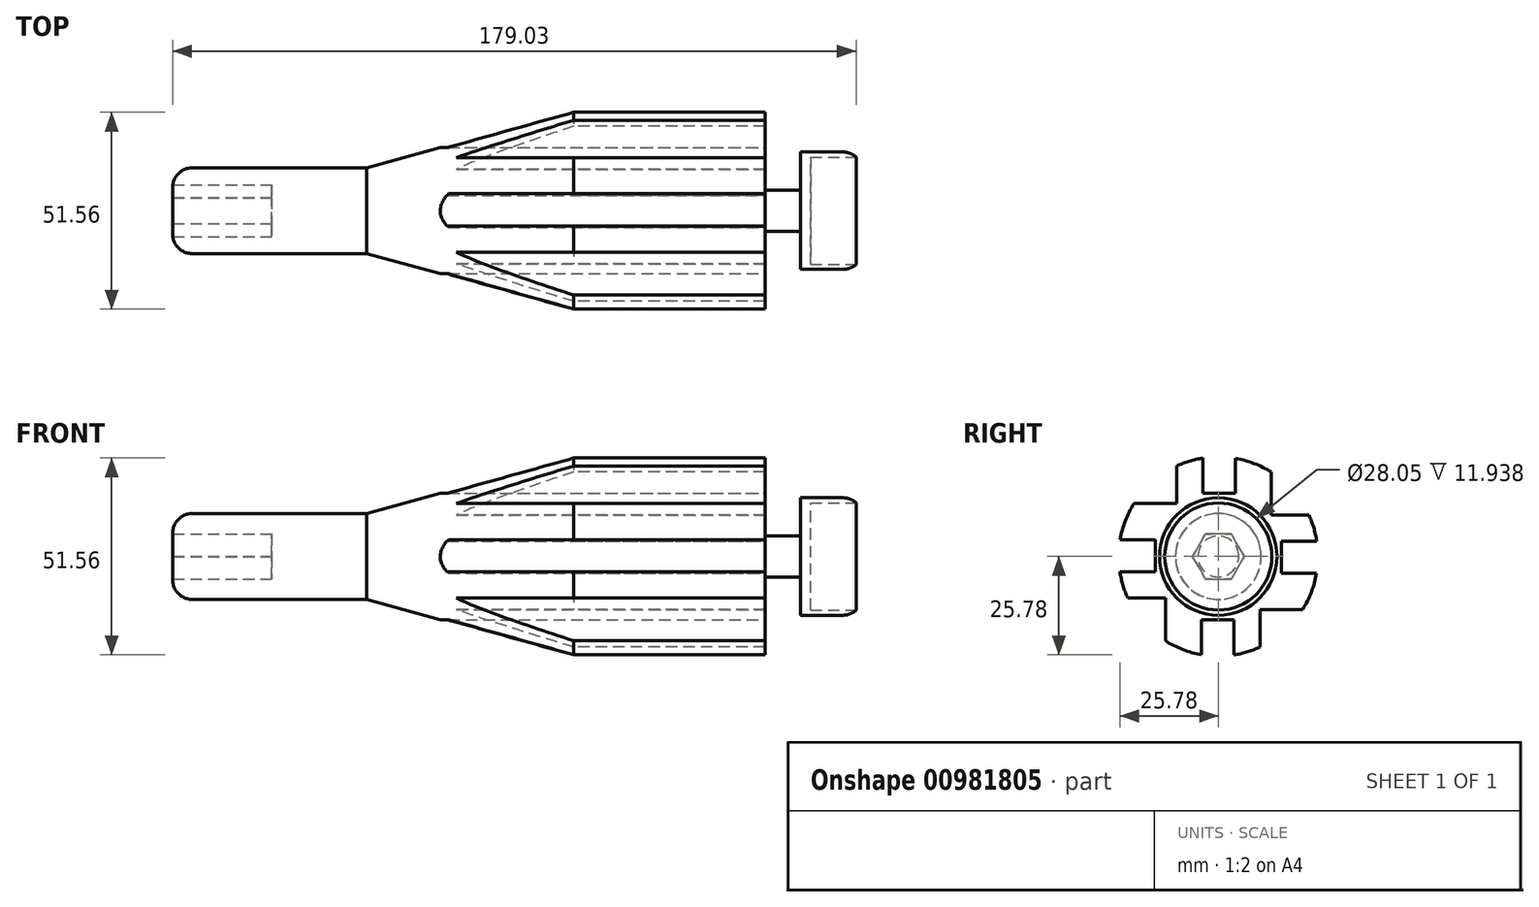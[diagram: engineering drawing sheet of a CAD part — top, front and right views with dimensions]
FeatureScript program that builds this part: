
annotation { "Feature Type Name" : "Feature", "Feature Type Description" : "" }
export const myFeature = defineFeature(function(context is Context, id is Id, definition is map)
    precondition{}
    {
        {
            var Q0;
            Q0=qCreatedBy(makeId("Front.planeOp"),FACE);
            var sketch = newSketch(context, id + "F0", { "sketchPlane" : qUnion([Q0])});
            skLineSegment(sketch, "E0", {"start": v(-55.13, 0) * mm, "end": v(-55.13, 11.23) * mm});
            skLineSegment(sketch, "E1", {"start": v(-55.13, 11.23) * mm, "end": v(-30.24, 11.23) * mm});
            skLineSegment(sketch, "E2", {"start": v(-30.24, 11.23) * mm, "end": v(24.02, 26.1) * mm});
            skLineSegment(sketch, "E3", {"start": v(24.02, 26.1) * mm, "end": v(74.14, 26.1) * mm});
            skLineSegment(sketch, "E4", {"start": v(74.14, 26.1) * mm, "end": v(74.14, 5.36) * mm});
            skLineSegment(sketch, "E5", {"start": v(74.14, 5.36) * mm, "end": v(83.47, 5.36) * mm});
            skLineSegment(sketch, "E6", {"start": v(83.47, 5.36) * mm, "end": v(83.47, 15.38) * mm});
            skLineSegment(sketch, "E7", {"start": v(83.47, 15.38) * mm, "end": v(97.99, 15.38) * mm});
            skLineSegment(sketch, "E8", {"start": v(97.99, 15.38) * mm, "end": v(97.99, 0) * mm});
            skLineSegment(sketch, "E9", {"start": v(-78.98, 0) * mm, "end": v(111.47, 0) * mm, "construction": true});
            skLineSegment(sketch, "E10", {"start": v(-55.13, 0) * mm, "end": v(97.99, 0) * mm});
            skSolve(sketch);
        }
        {
            var Q0;
            Q0=makeQuery(id+"F0.imprint","IMPRINT",FACE,{"disambiguationData":[TD([[makeQuery(id+"F0.imprint","IMPRINT",EDGE,{"derivedFrom":sQuery(id+"F0.wireOp",EDGE,"E0")}),-1.0]])]});
            var Q1;
            Q1=sQuery(id+"F0.wireOp",EDGE,"E9");
            revolve(context, id + "F1", {"surfaceOperationType" : NewSurfaceOperationType.NEW, "entities" : qUnion([Q0]), "axis" : qUnion([Q1]), "revolveType" : RevolveType.FULL});
        }
        {
            var Q0;
            Q0=makeQuery(id+"F1.opRevolve","SWEPT_FACE",FACE,{"disambiguationData":[OSD([sQuery(id+"F0.wireOp",EDGE,"E4")])]});
            var sketch = newSketch(context, id + "F2", { "sketchPlane" : qUnion([Q0])});
            skLineSegment(sketch, "E11.bottom", {"start": v(-4.05, 28.22) * mm, "end": v(4.44, 28.22) * mm});
            skLineSegment(sketch, "E11.top", {"start": v(-4.05, 16.52) * mm, "end": v(4.44, 16.52) * mm});
            skLineSegment(sketch, "E11.left", {"start": v(-4.05, 28.22) * mm, "end": v(-4.05, 16.52) * mm});
            skLineSegment(sketch, "E11.right", {"start": v(4.44, 28.22) * mm, "end": v(4.44, 16.52) * mm});
            skLineSegment(sketch, "E12.1.0", {"start": v(-28.22, -4.05) * mm, "end": v(-28.22, 4.44) * mm});
            skLineSegment(sketch, "E12.1.1", {"start": v(-16.52, -4.05) * mm, "end": v(-16.52, 4.44) * mm});
            skLineSegment(sketch, "E12.1.2", {"start": v(-28.22, 4.44) * mm, "end": v(-16.52, 4.44) * mm});
            skLineSegment(sketch, "E12.1.3", {"start": v(-28.22, -4.05) * mm, "end": v(-16.52, -4.05) * mm});
            skLineSegment(sketch, "E12.2.0", {"start": v(4.05, -28.22) * mm, "end": v(-4.44, -28.22) * mm});
            skLineSegment(sketch, "E12.2.1", {"start": v(4.05, -16.52) * mm, "end": v(-4.44, -16.52) * mm});
            skLineSegment(sketch, "E12.2.2", {"start": v(-4.44, -28.22) * mm, "end": v(-4.44, -16.52) * mm});
            skLineSegment(sketch, "E12.2.3", {"start": v(4.05, -28.22) * mm, "end": v(4.05, -16.52) * mm});
            skLineSegment(sketch, "E12.3.0", {"start": v(28.22, 4.05) * mm, "end": v(28.22, -4.44) * mm});
            skLineSegment(sketch, "E12.3.1", {"start": v(16.52, 4.05) * mm, "end": v(16.52, -4.44) * mm});
            skLineSegment(sketch, "E12.3.2", {"start": v(28.22, -4.44) * mm, "end": v(16.52, -4.44) * mm});
            skLineSegment(sketch, "E12.3.3", {"start": v(28.22, 4.05) * mm, "end": v(16.52, 4.05) * mm});
            skPoint(sketch, "E12.center", {"position": v(0, 0) * mm});
            skSolve(sketch);
        }
        {
            var Q0;
            {var subQ0=sQuery(id+"F2.wireOp",EDGE,"E11.top");Q0=makeQuery(id+"F2.imprint","IMPRINT",FACE,{"disambiguationData":[TD([[makeQuery(id+"F2.imprint","IMPRINT",EDGE,{"derivedFrom":subQ0}),1.0]])]});}
            var Q1;
            {var subQ0=sQuery(id+"F2.wireOp",EDGE,"E12.1.1");Q1=makeQuery(id+"F2.imprint","IMPRINT",FACE,{"disambiguationData":[TD([[makeQuery(id+"F2.imprint","IMPRINT",EDGE,{"derivedFrom":subQ0}),1.0]])]});}
            var Q2;
            {var subQ0=sQuery(id+"F2.wireOp",EDGE,"E12.2.0");Q2=makeQuery(id+"F2.imprint","IMPRINT",FACE,{"disambiguationData":[TD([[makeQuery(id+"F2.imprint","IMPRINT",EDGE,{"derivedFrom":subQ0}),-1.0]])]});}
            var Q3;
            {var subQ0=sQuery(id+"F2.wireOp",EDGE,"E12.2.1");Q3=makeQuery(id+"F2.imprint","IMPRINT",FACE,{"disambiguationData":[TD([[makeQuery(id+"F2.imprint","IMPRINT",EDGE,{"derivedFrom":subQ0}),1.0]])]});}
            var Q4;
            {var subQ0=sQuery(id+"F2.wireOp",EDGE,"E12.3.1");Q4=makeQuery(id+"F2.imprint","IMPRINT",FACE,{"disambiguationData":[TD([[makeQuery(id+"F2.imprint","IMPRINT",EDGE,{"derivedFrom":subQ0}),1.0]])]});}
            var Q5;
            Q5=sQuery(id+"F2.wireOp",EDGE,"E11.left");
            var Q6;
            Q6=sQuery(id+"F2.wireOp",EDGE,"E11.bottom");
            var Q7;
            Q7=sQuery(id+"F2.wireOp",EDGE,"E11.top");
            var Q8;
            Q8=sQuery(id+"F2.wireOp",EDGE,"E11.right");
            var Q9;
            Q9=sQuery(id+"F2.wireOp",EDGE,"E12.3.3");
            var Q10;
            Q10=sQuery(id+"F2.wireOp",EDGE,"E12.3.0");
            var Q11;
            Q11=sQuery(id+"F2.wireOp",EDGE,"E12.3.2");
            var Q12;
            Q12=sQuery(id+"F2.wireOp",EDGE,"E12.3.1");
            var Q13;
            Q13=sQuery(id+"F2.wireOp",EDGE,"E12.2.1");
            var Q14;
            Q14=sQuery(id+"F2.wireOp",EDGE,"E12.2.0");
            var Q15;
            Q15=sQuery(id+"F2.wireOp",EDGE,"E12.2.3");
            var Q16;
            Q16=sQuery(id+"F2.wireOp",EDGE,"E12.2.2");
            var Q17;
            Q17=sQuery(id+"F2.wireOp",EDGE,"E12.1.3");
            var Q18;
            Q18=sQuery(id+"F2.wireOp",EDGE,"E12.1.2");
            var Q19;
            Q19=sQuery(id+"F2.wireOp",EDGE,"E12.1.0");
            var Q20;
            Q20=sQuery(id+"F2.wireOp",EDGE,"E12.1.1");
            extrude(context, id + "F3", {"entities" : qUnion([Q0, Q1, Q2, Q3, Q4]), "operationType" : NewBodyOperationType.REMOVE, "surfaceEntities" : qUnion([Q5, Q6, Q7, Q8, Q9, Q10, Q11, Q12, Q13, Q14, Q15, Q16, Q17, Q18, Q19, Q20]), "endBound" : BoundingType.THROUGH_ALL, "oppositeDirection" : true, "depth" : 25.4 * mm, "offsetDistance" : 25.4 * mm});
        }
        {
            var Q0;
            Q0=makeQuery(id+"F1.opRevolve","SWEPT_FACE",FACE,{"disambiguationData":[OSD([sQuery(id+"F0.wireOp",EDGE,"E8")])]});
            var sketch = newSketch(context, id + "F4", { "sketchPlane" : qUnion([Q0])});
            skCircle(sketch, "E13", {"center": v(0, 0) * mm, "radius": 14.03 * mm});
            skSolve(sketch);
        }
        {
            var Q0;
            Q0 = qSketchRegion(id + "F4", true);
            extrude(context, id + "F5", {"entities" : qUnion([Q0]), "operationType" : NewBodyOperationType.REMOVE, "oppositeDirection" : true, "depth" : 11.94 * mm, "offsetDistance" : 25.4 * mm});
        }
        {
            var Q0;
            Q0=makeQuery(id+"F1.opRevolve","SWEPT_FACE",FACE,{"disambiguationData":[OSD([sQuery(id+"F0.wireOp",EDGE,"E4")])]});
            var sketch = newSketch(context, id + "F6", { "sketchPlane" : qUnion([Q0])});
            skLineSegment(sketch, "E14.bottom", {"start": v(13.88, 10.9) * mm, "end": v(23.77, 10.9) * mm});
            skLineSegment(sketch, "E14.top", {"start": v(13.88, 22.1) * mm, "end": v(23.77, 22.1) * mm});
            skLineSegment(sketch, "E14.left", {"start": v(13.88, 10.9) * mm, "end": v(13.88, 22.1) * mm});
            skLineSegment(sketch, "E14.right", {"start": v(23.77, 10.9) * mm, "end": v(23.77, 22.1) * mm});
            skLineSegment(sketch, "E15.1.0", {"start": v(-10.9, 13.88) * mm, "end": v(-10.9, 23.77) * mm});
            skLineSegment(sketch, "E15.1.1", {"start": v(-10.9, 23.77) * mm, "end": v(-22.1, 23.77) * mm});
            skLineSegment(sketch, "E15.1.2", {"start": v(-22.1, 13.88) * mm, "end": v(-22.1, 23.77) * mm});
            skLineSegment(sketch, "E15.1.3", {"start": v(-10.9, 13.88) * mm, "end": v(-22.1, 13.88) * mm});
            skLineSegment(sketch, "E15.2.0", {"start": v(-13.88, -10.9) * mm, "end": v(-23.77, -10.9) * mm});
            skLineSegment(sketch, "E15.2.1", {"start": v(-23.77, -10.9) * mm, "end": v(-23.77, -22.1) * mm});
            skLineSegment(sketch, "E15.2.2", {"start": v(-13.88, -22.1) * mm, "end": v(-23.77, -22.1) * mm});
            skLineSegment(sketch, "E15.2.3", {"start": v(-13.88, -10.9) * mm, "end": v(-13.88, -22.1) * mm});
            skLineSegment(sketch, "E15.3.0", {"start": v(10.9, -13.88) * mm, "end": v(10.9, -23.77) * mm});
            skLineSegment(sketch, "E15.3.1", {"start": v(10.9, -23.77) * mm, "end": v(22.1, -23.77) * mm});
            skLineSegment(sketch, "E15.3.2", {"start": v(22.1, -13.88) * mm, "end": v(22.1, -23.77) * mm});
            skLineSegment(sketch, "E15.3.3", {"start": v(10.9, -13.88) * mm, "end": v(22.1, -13.88) * mm});
            skPoint(sketch, "E15.center", {"position": v(0, 0) * mm});
            skSolve(sketch);
        }
        {
            var Q0;
            {var subQ0=sQuery(id+"F6.wireOp",EDGE,"E15.2.3");var subQ1=sQuery(id+"F6.wireOp",EDGE,"E15.2.0");var subQ2=makeQuery(id+"F6.imprint","INTERSECT",VERTEX,{"derivedFrom":[subQ1,subQ0]});Q0=makeQuery(id+"F6.imprint","IMPRINT",FACE,{"disambiguationData":[TD([[makeQuery(id+"F6.imprint","IMPRINT",EDGE,{"disambiguationData":[TD([[subQ2,-1.0]])],"derivedFrom":subQ1}),1.0]])]});}
            var Q1;
            {var subQ6=sQuery(id+"F6.wireOp",EDGE,"E15.2.1");Q1=makeQuery(id+"F6.imprint","IMPRINT",FACE,{"disambiguationData":[TD([[makeQuery(id+"F6.imprint","IMPRINT",EDGE,{"derivedFrom":subQ6}),1.0]])]});}
            var Q2;
            {var subQ6=sQuery(id+"F6.wireOp",EDGE,"E15.1.1");Q2=makeQuery(id+"F6.imprint","IMPRINT",FACE,{"disambiguationData":[TD([[makeQuery(id+"F6.imprint","IMPRINT",EDGE,{"derivedFrom":subQ6}),1.0]])]});}
            var Q3;
            {var subQ0=sQuery(id+"F6.wireOp",EDGE,"E15.1.3");var subQ1=sQuery(id+"F6.wireOp",EDGE,"E15.1.0");var subQ2=makeQuery(id+"F6.imprint","INTERSECT",VERTEX,{"derivedFrom":[subQ1,subQ0]});Q3=makeQuery(id+"F6.imprint","IMPRINT",FACE,{"disambiguationData":[TD([[makeQuery(id+"F6.imprint","IMPRINT",EDGE,{"disambiguationData":[TD([[subQ2,-1.0]])],"derivedFrom":subQ1}),1.0]])]});}
            var Q4;
            {var subQ0=sQuery(id+"F6.wireOp",EDGE,"E14.left");var subQ1=sQuery(id+"F6.wireOp",EDGE,"E14.bottom");var subQ2=makeQuery(id+"F6.imprint","INTERSECT",VERTEX,{"derivedFrom":[subQ1,subQ0]});Q4=makeQuery(id+"F6.imprint","IMPRINT",FACE,{"disambiguationData":[TD([[makeQuery(id+"F6.imprint","IMPRINT",EDGE,{"disambiguationData":[TD([[subQ2,-1.0]])],"derivedFrom":subQ1}),1.0]])]});}
            var Q5;
            {var subQ2=sQuery(id+"F6.wireOp",EDGE,"E14.top");Q5=makeQuery(id+"F6.imprint","IMPRINT",FACE,{"disambiguationData":[TD([[makeQuery(id+"F6.imprint","IMPRINT",EDGE,{"derivedFrom":subQ2}),-1.0]])]});}
            var Q6;
            {var subQ0=sQuery(id+"F6.wireOp",EDGE,"E15.3.3");var subQ1=sQuery(id+"F6.wireOp",EDGE,"E15.3.0");var subQ2=makeQuery(id+"F6.imprint","INTERSECT",VERTEX,{"derivedFrom":[subQ1,subQ0]});Q6=makeQuery(id+"F6.imprint","IMPRINT",FACE,{"disambiguationData":[TD([[makeQuery(id+"F6.imprint","IMPRINT",EDGE,{"disambiguationData":[TD([[subQ2,-1.0]])],"derivedFrom":subQ1}),1.0]])]});}
            var Q7;
            {var subQ6=sQuery(id+"F6.wireOp",EDGE,"E15.3.1");Q7=makeQuery(id+"F6.imprint","IMPRINT",FACE,{"disambiguationData":[TD([[makeQuery(id+"F6.imprint","IMPRINT",EDGE,{"derivedFrom":subQ6}),1.0]])]});}
            var Q8;
            Q8=sQuery(id+"F6.wireOp",EDGE,"E15.2.2");
            var Q9;
            Q9=sQuery(id+"F6.wireOp",EDGE,"E15.2.0");
            var Q10;
            Q10=sQuery(id+"F6.wireOp",EDGE,"E15.2.3");
            var Q11;
            Q11=sQuery(id+"F6.wireOp",EDGE,"E15.2.1");
            var Q12;
            Q12=sQuery(id+"F6.wireOp",EDGE,"E15.1.3");
            var Q13;
            Q13=sQuery(id+"F6.wireOp",EDGE,"E15.1.0");
            var Q14;
            Q14=sQuery(id+"F6.wireOp",EDGE,"E15.1.1");
            var Q15;
            Q15=sQuery(id+"F6.wireOp",EDGE,"E15.1.2");
            var Q16;
            Q16=sQuery(id+"F6.wireOp",EDGE,"E14.left");
            var Q17;
            Q17=sQuery(id+"F6.wireOp",EDGE,"E14.top");
            var Q18;
            Q18=sQuery(id+"F6.wireOp",EDGE,"E14.right");
            var Q19;
            Q19=sQuery(id+"F6.wireOp",EDGE,"E14.bottom");
            var Q20;
            Q20=sQuery(id+"F6.wireOp",EDGE,"E15.3.2");
            var Q21;
            Q21=sQuery(id+"F6.wireOp",EDGE,"E15.3.3");
            var Q22;
            Q22=sQuery(id+"F6.wireOp",EDGE,"E15.3.1");
            var Q23;
            Q23=sQuery(id+"F6.wireOp",EDGE,"E15.3.0");
            extrude(context, id + "F7", {"entities" : qUnion([Q0, Q1, Q2, Q3, Q4, Q5, Q6, Q7]), "operationType" : NewBodyOperationType.REMOVE, "surfaceEntities" : qUnion([Q8, Q9, Q10, Q11, Q12, Q13, Q14, Q15, Q16, Q17, Q18, Q19, Q20, Q21, Q22, Q23]), "endBound" : BoundingType.THROUGH_ALL, "oppositeDirection" : true, "depth" : 25.4 * mm, "offsetDistance" : 25.4 * mm});
        }
        {
            var Q0;
            Q0=makeQuery(id+"F1.opRevolve","SWEPT_FACE",FACE,{"disambiguationData":[OSD([sQuery(id+"F0.wireOp",EDGE,"E0")])]});
            var sketch = newSketch(context, id + "F8", { "sketchPlane" : qUnion([Q0])});
            skCircle(sketch, "E16.cCircle", {"center": v(0, 0) * mm, "radius": 5.9 * mm, "construction": true});
            skLineSegment(sketch, "E16.0", {"start": v(6.8, -0.02) * mm, "end": v(3.38, -5.9) * mm});
            skLineSegment(sketch, "E16.1", {"start": v(3.38, -5.9) * mm, "end": v(-3.42, -5.88) * mm});
            skLineSegment(sketch, "E16.2", {"start": v(-3.42, -5.88) * mm, "end": v(-6.8, 0.02) * mm});
            skLineSegment(sketch, "E16.3", {"start": v(-6.8, 0.02) * mm, "end": v(-3.38, 5.9) * mm});
            skLineSegment(sketch, "E16.4", {"start": v(-3.38, 5.9) * mm, "end": v(3.42, 5.88) * mm});
            skLineSegment(sketch, "E16.5", {"start": v(3.42, 5.88) * mm, "end": v(6.8, -0.02) * mm});
            skPoint(sketch, "E16.0.midPoint", {"position": v(5.1, -2.96) * mm});
            skSolve(sketch);
        }
        {
            var Q0;
            Q0=makeQuery(id+"F8.imprint","IMPRINT",FACE,{"disambiguationData":[TD([[makeQuery(id+"F8.imprint","IMPRINT",EDGE,{"derivedFrom":sQuery(id+"F8.wireOp",EDGE,"E16.0")}),1.0]])]});
            extrude(context, id + "F9", {"entities" : qUnion([Q0]), "operationType" : NewBodyOperationType.ADD, "depth" : 25.9 * mm, "offsetDistance" : 25.4 * mm});
        }
        {
            var Q0;
            Q0=makeQuery(id+"F9.opExtrude","CAP_EDGE",EDGE,{"disambiguationData":[OSD([sQuery(id+"F0.wireOp",EDGE,"E0"),sQuery(id+"F0.wireOp",EDGE,"E1")])],"isStart":false});
            fillet(context, id + "F10", {"entities" : qUnion([Q0]), "radius" : 5.08 * mm, "tangentPropagation" : true, "allowEdgeOverflow" : false});
        }
        {
            var Q0;
            Q0=makeQuery(id+"F1.opRevolve","SWEPT_EDGE",EDGE,{"disambiguationData":[OSD([sQuery(id+"F0.wireOp",EDGE,"E7"),sQuery(id+"F0.wireOp",EDGE,"E8")])]});
            fillet(context, id + "F11", {"entities" : qUnion([Q0]), "radius" : 5.08 * mm, "tangentPropagation" : true, "allowEdgeOverflow" : false});
        }
    });
